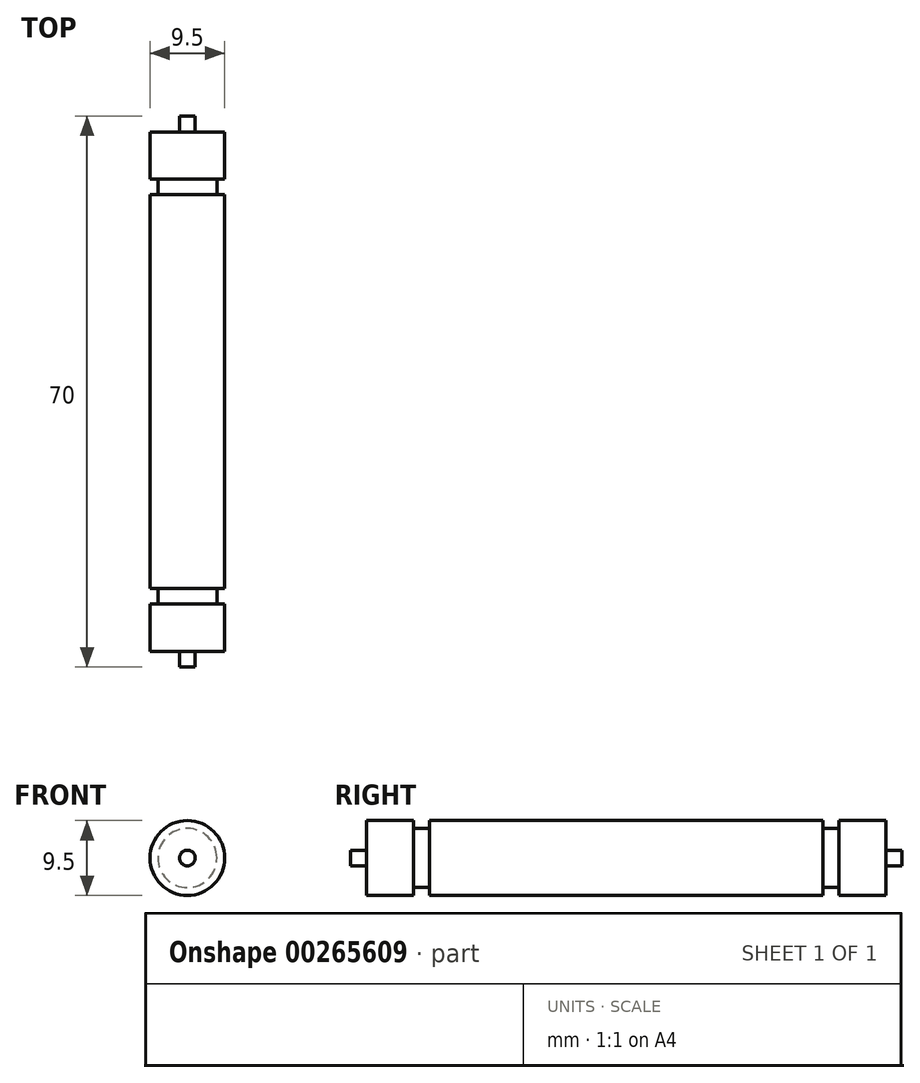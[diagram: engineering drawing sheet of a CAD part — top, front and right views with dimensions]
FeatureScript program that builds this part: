
annotation { "Feature Type Name" : "Feature", "Feature Type Description" : "" }
export const myFeature = defineFeature(function(context is Context, id is Id, definition is map)
    precondition{}
    {
        {
            var Q0;
            Q0=qCreatedBy(makeId("Front.planeOp"),FACE);
            var sketch = newSketch(context, id + "F0", { "sketchPlane" : qUnion([Q0])});
            skCircle(sketch, "E0", {"center": v(0, 0) * mm, "radius": 4.75 * mm});
            skSolve(sketch);
        }
        {
            var Q0;
            Q0 = qSketchRegion(id + "F0", true);
            var Q1;
            Q1=makeQuery(id+"F0.imprint","IMPRINT",FACE,{"disambiguationData":[TD([[makeQuery(id+"F0.imprint","IMPRINT",EDGE,{"derivedFrom":sQuery(id+"F0.wireOp",EDGE,"E0")}),1.0]])]});
            extrude(context, id + "F1", {"entities" : qUnion([Q0, Q1]), "depth" : 50 * mm});
        }
        {
            var Q0;
            Q0=makeQuery(id+"F1.opExtrude","CAP_FACE",FACE,{"disambiguationData":[OSD([sQuery(id+"F0.wireOp",EDGE,"E0")])],"isStart":false});
            var sketch = newSketch(context, id + "F2", { "sketchPlane" : qUnion([Q0])});
            skCircle(sketch, "E1", {"center": v(0, 0) * mm, "radius": 3.75 * mm});
            skSolve(sketch);
        }
        {
            var Q0;
            Q0=makeQuery(id+"F2.imprint","IMPRINT",FACE,{"disambiguationData":[TD([[makeQuery(id+"F2.imprint","IMPRINT",EDGE,{"derivedFrom":sQuery(id+"F2.wireOp",EDGE,"E1")}),1.0]])]});
            extrude(context, id + "F3", {"entities" : qUnion([Q0]), "operationType" : NewBodyOperationType.ADD, "depth" : 2 * mm});
        }
        {
            var Q0;
            Q0=makeQuery(id+"F1.opExtrude","CAP_FACE",FACE,{"disambiguationData":[OSD([sQuery(id+"F0.wireOp",EDGE,"E0")])],"isStart":true});
            var sketch = newSketch(context, id + "F4", { "sketchPlane" : qUnion([Q0])});
            skCircle(sketch, "E2", {"center": v(0, 0) * mm, "radius": 3.75 * mm});
            skSolve(sketch);
        }
        {
            var Q0;
            Q0=makeQuery(id+"F4.imprint","IMPRINT",FACE,{"disambiguationData":[TD([[makeQuery(id+"F4.imprint","IMPRINT",EDGE,{"derivedFrom":sQuery(id+"F4.wireOp",EDGE,"E2")}),1.0]])]});
            extrude(context, id + "F5", {"entities" : qUnion([Q0]), "operationType" : NewBodyOperationType.ADD, "depth" : 2 * mm});
        }
        {
            var Q0;
            Q0=makeQuery(id+"F3.opExtrude","CAP_FACE",FACE,{"disambiguationData":[OSD([sQuery(id+"F2.wireOp",EDGE,"E1")])],"isStart":false});
            var sketch = newSketch(context, id + "F6", { "sketchPlane" : qUnion([Q0])});
            skCircle(sketch, "E3", {"center": v(0, 0) * mm, "radius": 4.75 * mm});
            skSolve(sketch);
        }
        {
            var Q0;
            Q0=makeQuery(id+"F6.imprint","IMPRINT",FACE,{"disambiguationData":[TD([[makeQuery(id+"F6.imprint","IMPRINT",EDGE,{"derivedFrom":sQuery(id+"F6.wireOp",EDGE,"E3")}),1.0]])]});
            var Q1;
            Q1=makeQuery(id+"F6.imprint","IMPRINT",FACE,{"disambiguationData":[TD([[makeQuery(id+"F6.imprint","IMPRINT",EDGE,{"derivedFrom":makeQuery(id+"F3.opExtrude","CAP_EDGE",EDGE,{"disambiguationData":[OSD([sQuery(id+"F2.wireOp",EDGE,"E1")])],"isStart":false})}),1.0]])]});
            extrude(context, id + "F7", {"entities" : qUnion([Q0, Q1]), "depth" : 6 * mm});
        }
        {
            var Q0;
            Q0=makeQuery(id+"F5.opExtrude","CAP_FACE",FACE,{"disambiguationData":[OSD([sQuery(id+"F4.wireOp",EDGE,"E2")])],"isStart":false});
            var sketch = newSketch(context, id + "F8", { "sketchPlane" : qUnion([Q0])});
            skCircle(sketch, "E4", {"center": v(0, 0) * mm, "radius": 4.75 * mm});
            skSolve(sketch);
        }
        {
            var Q0;
            Q0=makeQuery(id+"F8.imprint","IMPRINT",FACE,{"disambiguationData":[TD([[makeQuery(id+"F8.imprint","IMPRINT",EDGE,{"derivedFrom":sQuery(id+"F8.wireOp",EDGE,"E4")}),1.0]])]});
            var Q1;
            Q1=makeQuery(id+"F8.imprint","IMPRINT",FACE,{"disambiguationData":[TD([[makeQuery(id+"F8.imprint","IMPRINT",EDGE,{"derivedFrom":makeQuery(id+"F5.opExtrude","CAP_EDGE",EDGE,{"disambiguationData":[OSD([sQuery(id+"F4.wireOp",EDGE,"E2")])],"isStart":false})}),1.0]])]});
            extrude(context, id + "F9", {"entities" : qUnion([Q0, Q1]), "operationType" : NewBodyOperationType.ADD, "depth" : 6 * mm});
        }
        {
            var Q0;
            Q0=makeQuery(id+"F9.opExtrude","CAP_FACE",FACE,{"disambiguationData":[OSD([sQuery(id+"F8.wireOp",EDGE,"E4")])],"isStart":false});
            var sketch = newSketch(context, id + "F10", { "sketchPlane" : qUnion([Q0])});
            skCircle(sketch, "E5", {"center": v(0, 0) * mm, "radius": 1 * mm});
            skSolve(sketch);
        }
        {
            var Q0;
            Q0=makeQuery(id+"F10.imprint","IMPRINT",FACE,{"disambiguationData":[TD([[makeQuery(id+"F10.imprint","IMPRINT",EDGE,{"derivedFrom":sQuery(id+"F10.wireOp",EDGE,"E5")}),1.0]])]});
            extrude(context, id + "F11", {"entities" : qUnion([Q0]), "operationType" : NewBodyOperationType.ADD, "depth" : 2 * mm});
        }
        {
            var Q0;
            Q0=makeQuery(id+"F7.opExtrude","CAP_FACE",FACE,{"disambiguationData":[OSD([sQuery(id+"F6.wireOp",EDGE,"E3")])],"isStart":false});
            var sketch = newSketch(context, id + "F12", { "sketchPlane" : qUnion([Q0])});
            skCircle(sketch, "E6", {"center": v(0, 0) * mm, "radius": 1 * mm});
            skSolve(sketch);
        }
        {
            var Q0;
            Q0=makeQuery(id+"F12.imprint","IMPRINT",FACE,{"disambiguationData":[TD([[makeQuery(id+"F12.imprint","IMPRINT",EDGE,{"derivedFrom":sQuery(id+"F12.wireOp",EDGE,"E6")}),1.0]])]});
            extrude(context, id + "F13", {"entities" : qUnion([Q0]), "operationType" : NewBodyOperationType.ADD, "depth" : 2 * mm});
        }
    });
